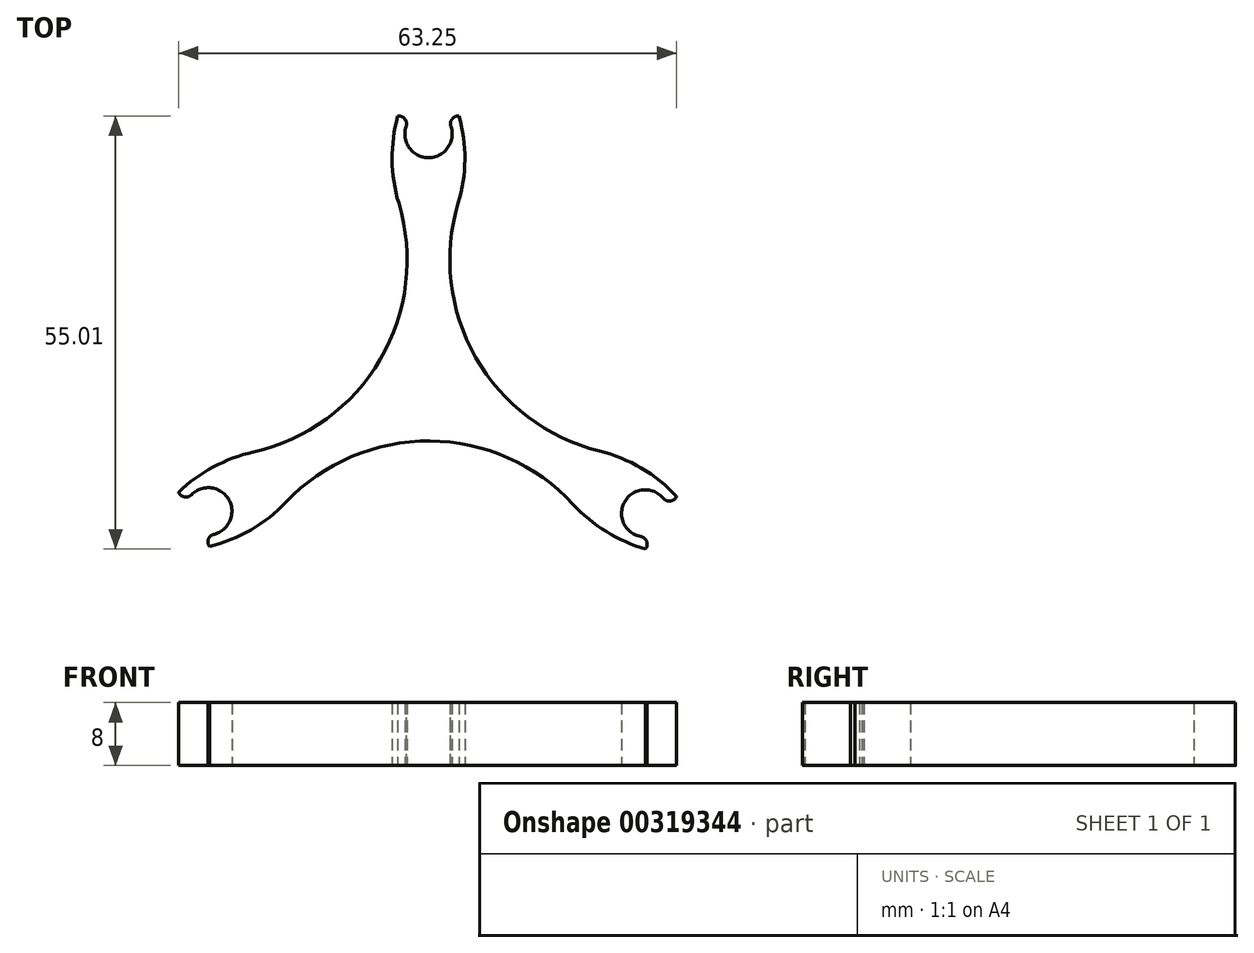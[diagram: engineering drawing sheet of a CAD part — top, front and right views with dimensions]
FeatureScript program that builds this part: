
annotation { "Feature Type Name" : "Feature", "Feature Type Description" : "" }
export const myFeature = defineFeature(function(context is Context, id is Id, definition is map)
    precondition{}
    {
        {
            var Q0;
            Q0=qCreatedBy(makeId("Top.planeOp"),FACE);
            var sketch = newSketch(context, id + "F0", { "sketchPlane" : qUnion([Q0])});
            skCircle(sketch, "E0", {"center": v(0, 0) * mm, "radius": 32 * mm, "construction": true});
            skArc(sketch, "E1", {"start": v(-1.72, 34.46) * mm, "mid": v(0, 29) * mm, "end": v(1.72, 34.46) * mm});
            skArc(sketch, "E2.1.0", {"start": v(-28.95, -18.77) * mm, "mid": v(-25.37, -14.45) * mm, "end": v(-30.91, -15.32) * mm});
            skArc(sketch, "E2.2.0", {"start": v(30.52, -16.09) * mm, "mid": v(24.94, -14.67) * mm, "end": v(28.89, -18.86) * mm});
            skPoint(sketch, "E2.center", {"position": v(-0.15, -0.04) * mm});
            skArc(sketch, "E3", {"start": v(-28.95, -18.77) * mm, "mid": v(-0.06, -34.5) * mm, "end": v(28.89, -18.86) * mm});
            skArc(sketch, "E4.trimOffspring", {"start": v(30.52, -16.09) * mm, "mid": v(29.98, 17.08) * mm, "end": v(1.72, 34.46) * mm});
            skArc(sketch, "E5.trimOffspring", {"start": v(-1.72, 34.46) * mm, "mid": v(-29.76, 17.45) * mm, "end": v(-30.91, -15.32) * mm});
            skCircle(sketch, "E6.1.0", {"center": v(-27.71, 16) * mm, "radius": 25 * mm});
            skCircle(sketch, "E6.3.0", {"center": v(0, -32) * mm, "radius": 25 * mm});
            skCircle(sketch, "E6.5.0", {"center": v(27.71, 16) * mm, "radius": 25 * mm});
            skSolve(sketch);
        }
        {
            var Q0;
            Q0=makeQuery(id+"F0.imprint","IMPRINT",FACE,{"disambiguationData":[TD([[makeQuery(id+"F0.imprint","IMPRINT",EDGE,{"derivedFrom":sQuery(id+"F0.wireOp",EDGE,"E1")}),-1.0]])]});
            extrude(context, id + "F1", {"entities" : qUnion([Q0]), "depth" : 8 * mm});
        }
        {
            var Q0;
            Q0=makeQuery(id+"F1.opExtrude","SWEPT_EDGE",EDGE,{"disambiguationData":[OSD([sQuery(id+"F0.wireOp",EDGE,"E2.1.0"),sQuery(id+"F0.wireOp",EDGE,"E5.trimOffspring")])]});
            var Q1;
            Q1=makeQuery(id+"F1.opExtrude","SWEPT_EDGE",EDGE,{"disambiguationData":[OSD([sQuery(id+"F0.wireOp",EDGE,"E2.1.0"),sQuery(id+"F0.wireOp",EDGE,"E3")])]});
            var Q2;
            Q2=makeQuery(id+"F1.opExtrude","SWEPT_EDGE",EDGE,{"disambiguationData":[OSD([sQuery(id+"F0.wireOp",EDGE,"E1"),sQuery(id+"F0.wireOp",EDGE,"E4.trimOffspring")])]});
            var Q3;
            Q3=makeQuery(id+"F1.opExtrude","SWEPT_EDGE",EDGE,{"disambiguationData":[OSD([sQuery(id+"F0.wireOp",EDGE,"E1"),sQuery(id+"F0.wireOp",EDGE,"E5.trimOffspring")])]});
            var Q4;
            Q4=makeQuery(id+"F1.opExtrude","SWEPT_EDGE",EDGE,{"disambiguationData":[OSD([sQuery(id+"F0.wireOp",EDGE,"E2.2.0"),sQuery(id+"F0.wireOp",EDGE,"E3")])]});
            var Q5;
            Q5=makeQuery(id+"F1.opExtrude","SWEPT_EDGE",EDGE,{"disambiguationData":[OSD([sQuery(id+"F0.wireOp",EDGE,"E2.2.0"),sQuery(id+"F0.wireOp",EDGE,"E4.trimOffspring")])]});
            fillet(context, id + "F2", {"entities" : qUnion([Q0, Q1, Q2, Q3, Q4, Q5]), "radius" : 1 * mm, "tangentPropagation" : true, "allowEdgeOverflow" : false});
        }
        {
            var Q0;
            {var subQ0=sQuery(id+"F0.wireOp",EDGE,"E6.1.0");var subQ1=sQuery(id+"F0.wireOp",EDGE,"E5.trimOffspring");Q0=makeQuery(id+"F1.opExtrude","SWEPT_EDGE",EDGE,{"disambiguationData":[OSD([subQ1,subQ0]),TDD([makeQuery(id+"F0.imprint","INTERSECT",VERTEX,{"disambiguationData":[OD(1.0)],"derivedFrom":[subQ1,subQ0]})])]});}
            var Q1;
            {var subQ0=sQuery(id+"F0.wireOp",EDGE,"E6.1.0");var subQ1=sQuery(id+"F0.wireOp",EDGE,"E5.trimOffspring");Q1=makeQuery(id+"F1.opExtrude","SWEPT_EDGE",EDGE,{"disambiguationData":[OSD([subQ1,subQ0]),TDD([makeQuery(id+"F0.imprint","INTERSECT",VERTEX,{"disambiguationData":[OD(0.0)],"derivedFrom":[subQ1,subQ0]})])]});}
            var Q2;
            {var subQ0=sQuery(id+"F0.wireOp",EDGE,"E6.5.0");var subQ1=sQuery(id+"F0.wireOp",EDGE,"E4.trimOffspring");Q2=makeQuery(id+"F1.opExtrude","SWEPT_EDGE",EDGE,{"disambiguationData":[OSD([subQ1,subQ0]),TDD([makeQuery(id+"F0.imprint","INTERSECT",VERTEX,{"disambiguationData":[OD(1.0)],"derivedFrom":[subQ1,subQ0]})])]});}
            var Q3;
            {var subQ0=sQuery(id+"F0.wireOp",EDGE,"E6.5.0");var subQ1=sQuery(id+"F0.wireOp",EDGE,"E4.trimOffspring");Q3=makeQuery(id+"F1.opExtrude","SWEPT_EDGE",EDGE,{"disambiguationData":[OSD([subQ1,subQ0]),TDD([makeQuery(id+"F0.imprint","INTERSECT",VERTEX,{"disambiguationData":[OD(0.0)],"derivedFrom":[subQ1,subQ0]})])]});}
            var Q4;
            {var subQ0=sQuery(id+"F0.wireOp",EDGE,"E6.3.0");var subQ1=sQuery(id+"F0.wireOp",EDGE,"E3");Q4=makeQuery(id+"F1.opExtrude","SWEPT_EDGE",EDGE,{"disambiguationData":[OSD([subQ1,subQ0]),TDD([makeQuery(id+"F0.imprint","INTERSECT",VERTEX,{"disambiguationData":[OD(1.0)],"derivedFrom":[subQ1,subQ0]})])]});}
            var Q5;
            {var subQ0=sQuery(id+"F0.wireOp",EDGE,"E6.3.0");var subQ1=sQuery(id+"F0.wireOp",EDGE,"E3");Q5=makeQuery(id+"F1.opExtrude","SWEPT_EDGE",EDGE,{"disambiguationData":[OSD([subQ1,subQ0]),TDD([makeQuery(id+"F0.imprint","INTERSECT",VERTEX,{"disambiguationData":[OD(0.0)],"derivedFrom":[subQ1,subQ0]})])]});}
            fillet(context, id + "F3", {"entities" : qUnion([Q0, Q1, Q2, Q3, Q4, Q5]), "radius" : 20 * mm, "tangentPropagation" : true, "allowEdgeOverflow" : false});
        }
    });
